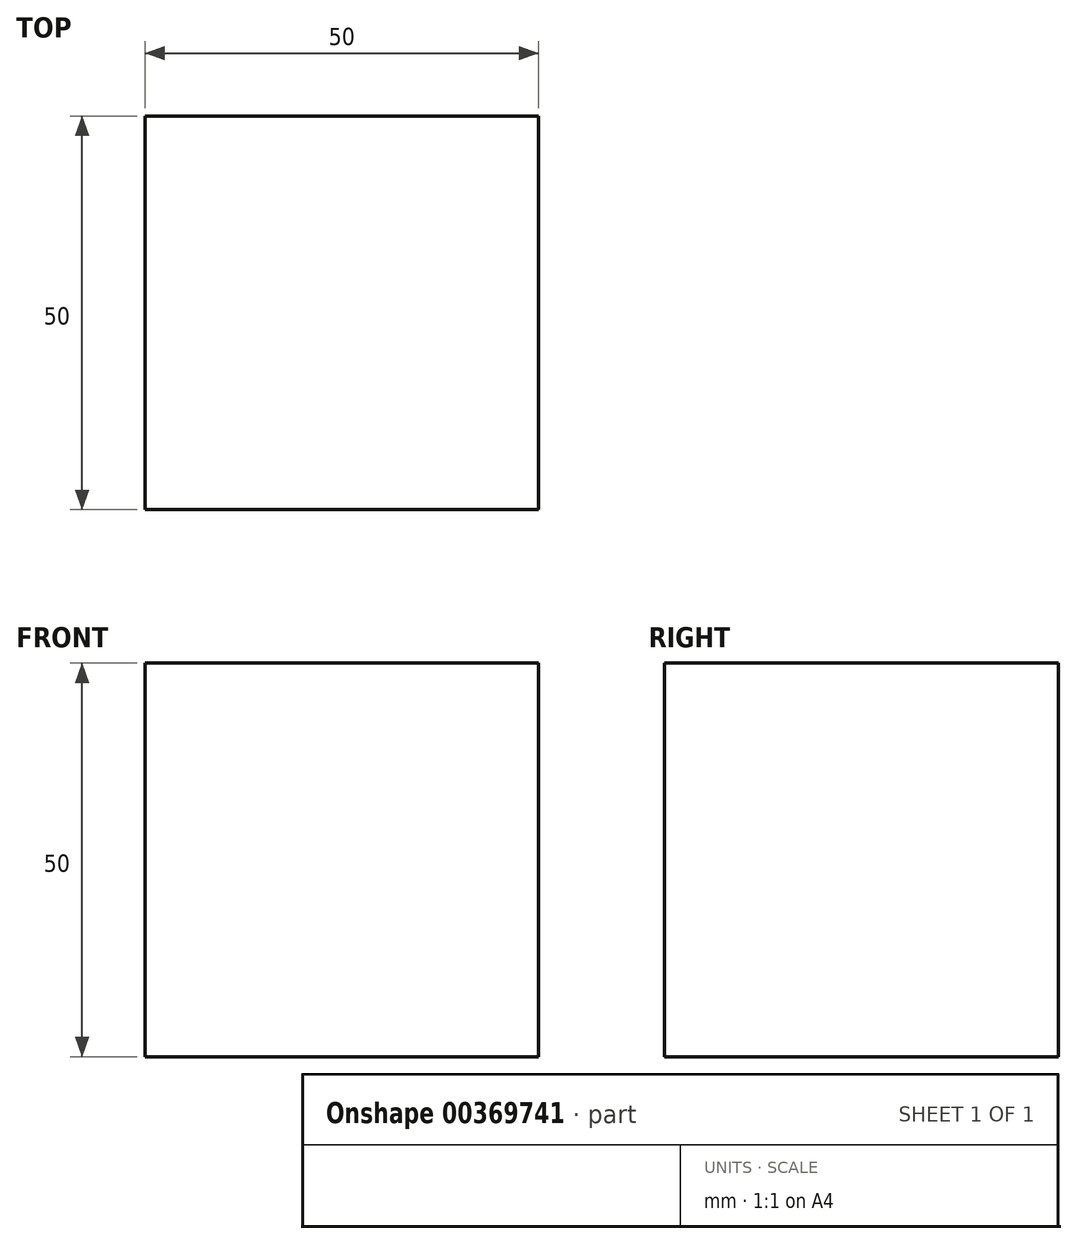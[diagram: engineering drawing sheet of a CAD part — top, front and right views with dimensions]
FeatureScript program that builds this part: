
annotation { "Feature Type Name" : "Feature", "Feature Type Description" : "" }
export const myFeature = defineFeature(function(context is Context, id is Id, definition is map)
    precondition{}
    {
        {
            var Q0;
            Q0=qCreatedBy(makeId("Front.planeOp"),FACE);
            var sketch = newSketch(context, id + "F0", { "sketchPlane" : qUnion([Q0])});
            skLineSegment(sketch, "E0.bottom", {"start": v(0, 0) * mm, "end": v(-50, 0) * mm});
            skLineSegment(sketch, "E0.top", {"start": v(0, 50) * mm, "end": v(-50, 50) * mm});
            skLineSegment(sketch, "E0.left", {"start": v(0, 0) * mm, "end": v(0, 50) * mm});
            skLineSegment(sketch, "E0.right", {"start": v(-50, 0) * mm, "end": v(-50, 50) * mm});
            skSolve(sketch);
        }
        {
            var Q0;
            Q0 = qSketchRegion(id + "F0", true);
            extrude(context, id + "F1", {"entities" : qUnion([Q0]), "depth" : 50 * mm});
        }
    });
